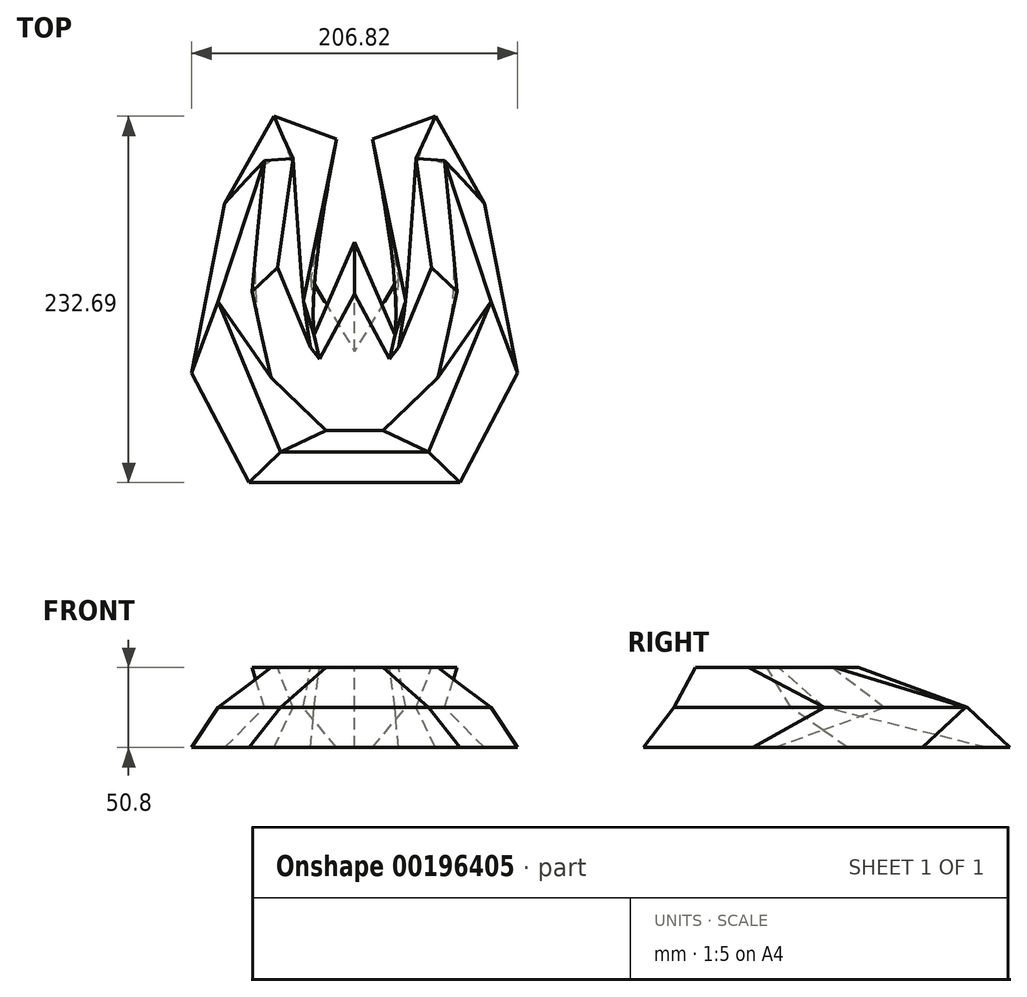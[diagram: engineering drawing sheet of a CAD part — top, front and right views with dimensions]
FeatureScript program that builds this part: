
annotation { "Feature Type Name" : "Feature", "Feature Type Description" : "" }
export const myFeature = defineFeature(function(context is Context, id is Id, definition is map)
    precondition{}
    {
        {
            var Q0;
            Q0=qCreatedBy(makeId("Top.planeOp"),FACE);
            var sketch = newSketch(context, id + "F0", { "sketchPlane" : qUnion([Q0])});
            skLineSegment(sketch, "E0", {"start": v(-51.27, 123.79) * mm, "end": v(-82.56, 68.39) * mm});
            skLineSegment(sketch, "E1", {"start": v(-82.56, 68.39) * mm, "end": v(-103.41, -39.16) * mm});
            skLineSegment(sketch, "E2", {"start": v(-103.41, -39.16) * mm, "end": v(-66.91, -108.9) * mm});
            skLineSegment(sketch, "E3", {"start": v(-51.27, 123.79) * mm, "end": v(-11.51, 109.45) * mm});
            skLineSegment(sketch, "E4", {"start": v(-11.51, 109.45) * mm, "end": v(-27.8, 20.8) * mm});
            skLineSegment(sketch, "E5", {"start": v(-27.8, 20.8) * mm, "end": v(0, -25.47) * mm});
            skLineSegment(sketch, "E6.MirrorCS", {"start": v(27.8, 20.8) * mm, "end": v(0, -25.47) * mm});
            skLineSegment(sketch, "E7.MirrorCS", {"start": v(11.51, 109.45) * mm, "end": v(27.8, 20.8) * mm});
            skLineSegment(sketch, "E8.MirrorCS", {"start": v(51.27, 123.79) * mm, "end": v(11.51, 109.45) * mm});
            skLineSegment(sketch, "E9.MirrorCS", {"start": v(51.27, 123.79) * mm, "end": v(82.56, 68.39) * mm});
            skLineSegment(sketch, "E10.MirrorCS", {"start": v(82.56, 68.39) * mm, "end": v(103.41, -39.16) * mm});
            skLineSegment(sketch, "E11.MirrorCS", {"start": v(103.41, -39.16) * mm, "end": v(66.91, -108.9) * mm});
            skLineSegment(sketch, "E12", {"start": v(-66.91, -108.9) * mm, "end": v(66.91, -108.9) * mm});
            skSolve(sketch);
        }
        {
            var Q0;
            Q0=qCreatedBy(makeId("Top.planeOp"),FACE);
            cPlane(context, id + "F1", {"entities" : qUnion([Q0]), "cplaneType" : CPlaneType.OFFSET, "offset" : 25.4 * mm, "width" : 152.4 * mm, "height" : 152.4 * mm});
        }
        {
            var Q0;
            Q0=qCreatedBy(id+"F1.planeOp",FACE);
            var sketch = newSketch(context, id + "F2", { "sketchPlane" : qUnion([Q0])});
            skLineSegment(sketch, "E13", {"start": v(-32.58, 6.28) * mm, "end": v(-39.1, 97.03) * mm});
            skLineSegment(sketch, "E14", {"start": v(-39.1, 97.03) * mm, "end": v(-57.25, 95.72) * mm});
            skLineSegment(sketch, "E15", {"start": v(-57.25, 95.72) * mm, "end": v(-86.56, 6.28) * mm});
            skLineSegment(sketch, "E16", {"start": v(-86.56, 6.28) * mm, "end": v(-47, -89.59) * mm});
            skLineSegment(sketch, "E17.MirrorCS", {"start": v(32.58, 6.28) * mm, "end": v(39.1, 97.03) * mm});
            skLineSegment(sketch, "E18.MirrorCS", {"start": v(39.1, 97.03) * mm, "end": v(57.25, 95.72) * mm});
            skLineSegment(sketch, "E19.MirrorCS", {"start": v(57.25, 95.72) * mm, "end": v(86.56, 6.28) * mm});
            skLineSegment(sketch, "E20.MirrorCS", {"start": v(86.56, 6.28) * mm, "end": v(47, -89.59) * mm});
            skLineSegment(sketch, "E21", {"start": v(-47, -89.59) * mm, "end": v(47, -89.59) * mm});
            skLineSegment(sketch, "E22", {"start": v(-32.58, 6.28) * mm, "end": v(-25.58, -15.08) * mm});
            skLineSegment(sketch, "E23", {"start": v(-25.58, -15.08) * mm, "end": v(0, 43.98) * mm});
            skPoint(sketch, "E24.start.orphan", {"position": v(0, 43.98) * mm});
            skLineSegment(sketch, "E25.MirrorCS", {"start": v(32.58, 6.28) * mm, "end": v(25.58, -15.08) * mm});
            skLineSegment(sketch, "E26.MirrorCS", {"start": v(25.58, -15.08) * mm, "end": v(0, 43.98) * mm});
            skSolve(sketch);
        }
        {
            var Q0;
            Q0=makeQuery(id+"F0.imprint","IMPRINT",FACE,{"disambiguationData":[TD([[makeQuery(id+"F0.imprint","IMPRINT",EDGE,{"derivedFrom":sQuery(id+"F0.wireOp",EDGE,"E0")}),1.0]])]});
            var Q1;
            Q1=makeQuery(id+"F2.imprint","IMPRINT",FACE,{"disambiguationData":[TD([[makeQuery(id+"F2.imprint","IMPRINT",EDGE,{"derivedFrom":sQuery(id+"F2.wireOp",EDGE,"E13")}),1.0]])]});
            loft(context, id + "F3", {"sheetProfilesArray" : [{ "sheetProfileEntities" : qUnion([Q0]) }, { "sheetProfileEntities" : qUnion([Q1]) }]});
        }
        {
            var Q0;
            Q0=makeQuery(id+"F3.opLoft","CAP_FACE",FACE,{"disambiguationData":[OSD([makeQuery(id+"F2.imprint","IMPRINT",FACE,{"disambiguationData":[TD([[makeQuery(id+"F2.imprint","IMPRINT",EDGE,{"derivedFrom":sQuery(id+"F2.wireOp",EDGE,"E13")}),1.0]])]})])],"isStart":true});
            cPlane(context, id + "F4", {"entities" : qUnion([Q0]), "cplaneType" : CPlaneType.OFFSET, "offset" : 25.4 * mm, "width" : 152.4 * mm, "height" : 152.4 * mm});
        }
        {
            var Q0;
            Q0=qCreatedBy(id+"F4.planeOp",FACE);
            var sketch = newSketch(context, id + "F5", { "sketchPlane" : qUnion([Q0])});
            skLineSegment(sketch, "E27", {"start": v(0, 10.93) * mm, "end": v(-22.34, -30.48) * mm});
            skLineSegment(sketch, "E28", {"start": v(-22.34, -30.48) * mm, "end": v(-27.92, -23.04) * mm});
            skLineSegment(sketch, "E29", {"start": v(-27.92, -23.04) * mm, "end": v(-48.86, 27.69) * mm});
            skLineSegment(sketch, "E30", {"start": v(-48.86, 27.69) * mm, "end": v(-65.15, 12.33) * mm});
            skLineSegment(sketch, "E31", {"start": v(-65.15, 12.33) * mm, "end": v(-53.05, -42.12) * mm});
            skLineSegment(sketch, "E32", {"start": v(-53.05, -42.12) * mm, "end": v(-18.15, -75.62) * mm});
            skLineSegment(sketch, "E33.MirrorCS", {"start": v(0, 10.93) * mm, "end": v(22.34, -30.48) * mm});
            skLineSegment(sketch, "E34.MirrorCS", {"start": v(22.34, -30.48) * mm, "end": v(27.92, -23.04) * mm});
            skLineSegment(sketch, "E35.MirrorCS", {"start": v(27.92, -23.04) * mm, "end": v(48.86, 27.69) * mm});
            skLineSegment(sketch, "E36.MirrorCS", {"start": v(48.86, 27.69) * mm, "end": v(65.15, 12.33) * mm});
            skLineSegment(sketch, "E37.MirrorCS", {"start": v(65.15, 12.33) * mm, "end": v(53.05, -42.12) * mm});
            skLineSegment(sketch, "E38.MirrorCS", {"start": v(53.05, -42.12) * mm, "end": v(18.15, -75.62) * mm});
            skLineSegment(sketch, "E39", {"start": v(-18.15, -75.62) * mm, "end": v(18.15, -75.62) * mm});
            skSolve(sketch);
        }
        {
            var Q1;
            Q1=makeQuery(id+"F3.opLoft","CAP_FACE",FACE,{"disambiguationData":[OSD([makeQuery(id+"F2.imprint","IMPRINT",FACE,{"disambiguationData":[TD([[makeQuery(id+"F2.imprint","IMPRINT",EDGE,{"derivedFrom":sQuery(id+"F2.wireOp",EDGE,"E13")}),1.0]])]})])],"isStart":true});
            var Q2;
            Q2=makeQuery(id+"F5.imprint","IMPRINT",FACE,{"disambiguationData":[TD([[makeQuery(id+"F5.imprint","IMPRINT",EDGE,{"derivedFrom":sQuery(id+"F5.wireOp",EDGE,"E27")}),1.0]])]});
            loft(context, id + "F6", {"operationType" : NewBodyOperationType.ADD, "sheetProfilesArray" : [{ "sheetProfileEntities" : qUnion([Q1]) }, { "sheetProfileEntities" : qUnion([Q2]) }]});
        }
    });
